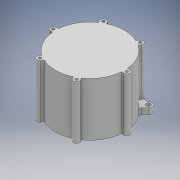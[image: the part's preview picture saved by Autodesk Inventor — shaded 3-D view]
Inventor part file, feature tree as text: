
AUTODESK INVENTOR PART (.ipt)
format: ipt  version: 2019.3 (Build 233278000, 278)  size: 377,856 bytes
history: native  units: mm
features: extrude x8, sketch x7, hole x6, pattern_circular x1, mirror x1, fillet x1
ambient origin geometry x8: Origin, YZ Plane, XZ Plane, XY Plane, X Axis, Y Axis, Z Axis, Center Point
bodies: Solid3 (feature_tree), Solid4 (feature_tree)
feature tree (24):
  sketch  "Sketch1"  dims[d1=66.0mm d2=132.0mm]
  extrude  "Extrusion5"  Depth=66.0mm
  extrude  "Extrusion6"  Depth=19.5mm
  hole  "Hole3"  [1 undecoded]
  hole  "Hole4"  [1 undecoded]
  pattern_circular  "Circular Pattern1"  [2 undecoded]
  mirror  "Mirror1"
  extrude  "Extrusion7"  Depth=4.0mm
  sketch  "Sketch2"  dims[d3=19.5mm d4=19.5mm]
  extrude  "Extrusion8"  Depth=11.0mm TaperAngle=0.0deg
  hole  "Hole8"  [1 undecoded]
  hole  "Hole9"  [1 undecoded]
  hole  "Hole10"  [1 undecoded]
  fillet  "Fillet1"  Radius=9.5mm
  extrude  "Extrusion10"  Depth=3.7mm TaperAngle=0.0deg
  extrude  "Extrusion12"  Depth=15.0mm
  extrude  "Extrusion13"  Depth=10.0mm
  extrude  "Extrusion14"  Depth=4.0mm
  hole  "Hole11"  [1 undecoded]
  sketch  "Sketch4"  dims[d6=104.0mm d16=4.0mm]
  sketch  "Sketch7"  dims[d19=10.5mm d40=13.0mm]
  sketch  "Sketch8"  dims[d43=10.5mm]
  sketch  "Sketch9"  dims[d44=5.25mm]
  sketch  "Sketch10"  dims[d45=7.748111mm d46=4.0mm d53=5.0mm d54=6.0mm d55=4.0mm d56=2.0mm d57=90.0deg d58=8.0mm d59=20.594885mm d60=8.0mm d61=6.0mm d62=4.0mm d63=2.0mm d64=90.0deg d65=8.0mm d66=20.594885mm d67=4.0mm d68=11.0mm d69=0.0mm d70=11.0mm d71=0.0mm d72=60.0mm d73=360.0deg d75=11.0mm d76=0.0mm d78=9.5mm d79=3.7mm d80=0.0mm d102=9.5mm d103=6.0mm d104=4.0mm d105=2.0mm d106=90.0deg d107=8.0mm d108=20.594885mm d109=8.5mm d110=6.0mm d111=4.0mm d112=2.0mm d113=90.0deg d114=8.0mm d115=20.594885mm d116=4.5mm d117=6.0mm d118=4.0mm d119=2.0mm d120=90.0deg d121=8.0mm d122=20.594885mm d123=15.0mm d124=10.0mm d126=114.0mm d129=3.7mm d130=0.0mm d133=85.0mm d134=0.0mm d135=50.0mm d136=5.0mm d137=0.0mm d138=12.0mm d139=22.5mm d140=0.0mm d141=21.0mm d142=6.0mm d143=6.0mm d144=4.0mm d145=2.0mm d146=90.0deg d147=12.0mm d148=20.594885mm d149=30.0mm d151=180.0deg d33=1.0mm d34=1.0mm d81=1.0mm d82=1.0mm d88=1.0mm d89=1.0mm]
note: 8 required parameter values undecoded (feature->parameter linkage not recoverable at this tier; creation-order binding heuristic only, values carry confidence <= 0.55)
